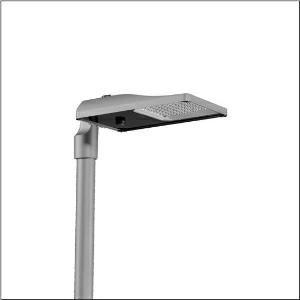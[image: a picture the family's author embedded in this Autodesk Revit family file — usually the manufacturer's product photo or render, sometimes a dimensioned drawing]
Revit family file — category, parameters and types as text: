
# Revit family: streetlight_sl_31_midi___st0_5a_5xh7b4at08la_3b68
name_source: partatom
category: Lighting Fixtures
units: mm (PartAtom-declared; Revit-internal decimal feet)

## family parameters
Cut with Voids When Loaded = No
Host = Face
Light Source = No
Part Type = Normal
Room Calculation Point = No
Round Connector Dimension = Use Diameter
Shared = No

## types (1)
- --- (1 x LED, 13610 lm, 86.5 W, 4000K)
    Apparent Load = 87 VA
    CIE Flux Codes = 41 75 97 100 100
    Color Rendering = 70
    Color Temperature = 4000K
    Default Elevation = 1800 mm
    Description = Streetlight SL 31 midi, mast luminaire, primary light control with lens, of PMMA, primary optical cover: cover, of toughened safety glass, transparent, light distribution: ST0.5a, light emission: direct distribution, primary light characteristic: asymmetric, installation type: post-top, side-entry, LED, High Power LED, rated luminous flux: 13.610lm, luminous efficacy: 157lm/W, light colour: 740, colour temperature: 4000K, control: presetting dimming logarithmic, flexible luminous flux parameterisation, time-dependent luminous flux control, constant luminous flux control, power reduction, intelligent temperature release in ECG and LED module, overheat protection, with cable H07RN-F 2x 1.5mm², mains connection: 220..240V, AC, 50/60Hz, connection cable pre-assembled, cable length: 10,5m, start of lifetime: 87W, end of service life: 90W, reduction: 40W, luminaire housing, of diecast aluminium, powder-coated, Siteco® metallic grey (DB 702S), corrosivity category C5 high according to DIN EN ISO 12944, sealing non-destructively replaceable, multi-level sealing system, mast flange (76/60mm) included as standard, inclination: -15°..+20° (post-top) | -20°..+20° (side-entry), adjustable in 5° steps, no sealing on luminaire upper side, Smart Interface below and above, protection rating (complete): IP66, insulation class (complete): insulation class II (safety insulation), certification: CE, ENEC, ENEC+, VDE, UKCA, ZD4i, impact resistance: IK09, permissible operating ambient temperature for outdoor applications: -40..+50°C, standard-compliant lighting for roads and squares, packaging unit: 1 piece

Light Distribution: ST0.5a
    Height = 79 mm
    Lamp = 1 x LED
    Lamp Light Flux = 13610 lm
    Lamp Power = 86.5 W
    Lamp count = 1
    Length = 577 mm
    Luminous efficacy = 157 lm/W
    Manufacturer = Siteco
    ModVariant = No
    Model = 5XH7B4AT08LA
    Number of Poles = 1
    OnlyDefault = Yes
    Power Factor = 1
    Product Name = Streetlight SL 31 midi | ST0.5a
    Product group = mast luminaire | pylon top
    ProductGroupID = 6100
    Protection Class = Protection class II
    Protection Degree = IP 66
    RLX_Detail_Level = 1
    RLX_Emergency_Light_Flux = 0 lm
    RLX_Emergency_Type = 0
    RLX_Emergency_Type_DB = No
    RlxData = <blob elided: 53917 chars, md5=dc4b454e>
    Socket = socket
    Standby Power = 0 W
    System Light Flux = 13610 lm
    System Power = 87 W
    Type Comments = factory setting: luminous flux: 100 % | dim-lin: 254 | 456 mA
    Type Image = l_1300321.jpg
    URL = http://relux.com
    VarID = @adj_016395
    Voltage = 0 V
    Weight = 0.00 kg
    Width = 362 mm

## geometry (parser evidence)
native form markers: Blend x4, Sweep x10
no freeform markers — native parametric forms only
